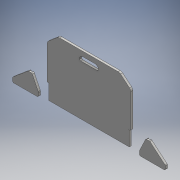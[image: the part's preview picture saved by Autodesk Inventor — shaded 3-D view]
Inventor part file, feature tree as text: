
AUTODESK INVENTOR PART (.ipt)
format: ipt  version: 2016 (Build 200138000, 138)  size: 222,208 bytes
history: native  units: mm
features: other x4, extrude x3, sketch x3, mirror x2, fillet x1
ambient origin geometry x8: Origin, YZ Plane, XZ Plane, XY Plane, X Axis, Y Axis, Z Axis, Center Point
bodies: Body1 (feature_tree), Body2 (feature_tree), Body3 (feature_tree)
feature tree (13):
  other  "back"
  extrude  "Extrusion1"  Depth=40.0mm
  mirror  "Mirror1"
  extrude  "Extrusion2"  Depth=120.0mm
  extrude  "Extrusion3"  Depth=17.5mm TaperAngle=0.0deg
  fillet  "Fillet1"  Radius=12.5mm
  mirror  "Mirror2"
  sketch  "Sketch1"  dims[d0=40.0mm d1=40.0mm]
  sketch  "Sketch2"  dims[d2=24.43461mm d4=120.0mm]
  sketch  "Sketch3"  dims[d5=508.0mm d6=17.5mm d7=0.0mm d8=12.5mm d9=355.6mm d10=32.5mm d11=70.0mm d12=150.0mm d13=75.0mm d14=20.0mm d15=17.5mm d16=0.0mm d17=5.0mm d18=0.0mm d19=18.135mm d21=30.0mm d23=130.0mm d24=6.35mm d25=6.35mm d27=10.0mm d28=20.0mm d29=24.43461mm d30=20.0mm]
  other  "foot"
  other  "Pattern of foot:1"
  other  "foot_flipped"
